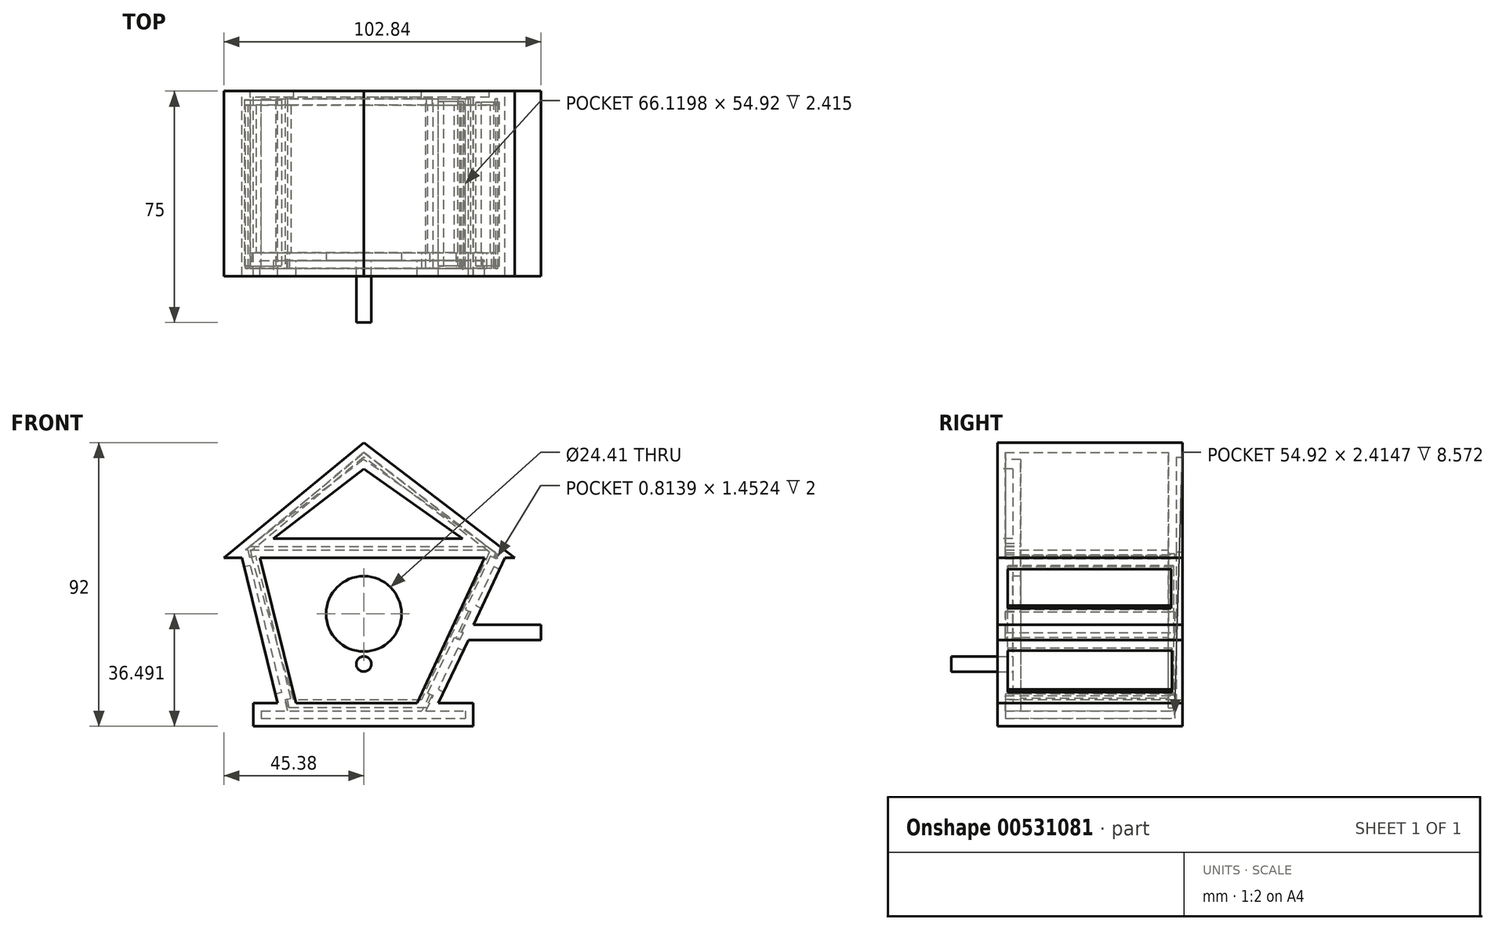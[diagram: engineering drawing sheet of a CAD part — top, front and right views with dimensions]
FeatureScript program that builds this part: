
annotation { "Feature Type Name" : "Feature", "Feature Type Description" : "" }
export const myFeature = defineFeature(function(context is Context, id is Id, definition is map)
    precondition{}
    {
        {
            var Q0;
            Q0=qCreatedBy(makeId("Front.planeOp"),FACE);
            var sketch = newSketch(context, id + "F0", { "sketchPlane" : qUnion([Q0])});
            skLineSegment(sketch, "E0.bottom", {"start": v(-35.75, -20.45) * mm, "end": v(35.45, -20.45) * mm});
            skLineSegment(sketch, "E0.top", {"start": v(-35.75, -27.94) * mm, "end": v(35.45, -27.94) * mm});
            skLineSegment(sketch, "E0.left", {"start": v(-35.75, -20.45) * mm, "end": v(-35.75, -27.94) * mm});
            skLineSegment(sketch, "E0.right", {"start": v(35.45, -20.45) * mm, "end": v(35.45, -27.94) * mm});
            skLineSegment(sketch, "E1", {"start": v(-27.88, -20.45) * mm, "end": v(-39.5, 26.72) * mm});
            skLineSegment(sketch, "E2", {"start": v(-39.5, 26.72) * mm, "end": v(-33.95, 28.09) * mm});
            skLineSegment(sketch, "E3", {"start": v(-33.95, 28.09) * mm, "end": v(-22, -20.45) * mm});
            skLineSegment(sketch, "E4", {"start": v(24.16, -20.45) * mm, "end": v(33.95, 0) * mm});
            skLineSegment(sketch, "E5", {"start": v(33.95, 0) * mm, "end": v(57.46, 0) * mm});
            skLineSegment(sketch, "E6", {"start": v(57.46, 0) * mm, "end": v(57.46, 4.97) * mm});
            skLineSegment(sketch, "E7", {"start": v(57.46, 4.97) * mm, "end": v(35.59, 4.97) * mm});
            skLineSegment(sketch, "E8", {"start": v(35.59, 4.97) * mm, "end": v(46.36, 28.15) * mm});
            skLineSegment(sketch, "E9", {"start": v(46.36, 28.15) * mm, "end": v(40.98, 30.65) * mm});
            skLineSegment(sketch, "E10", {"start": v(40.98, 30.65) * mm, "end": v(17.23, -20.45) * mm});
            skLineSegment(sketch, "E11", {"start": v(-45.38, 26.72) * mm, "end": v(48.97, 26.72) * mm});
            skLineSegment(sketch, "E12", {"start": v(48.97, 26.72) * mm, "end": v(0, 64.06) * mm});
            skLineSegment(sketch, "E13", {"start": v(0, 64.06) * mm, "end": v(-45.38, 26.72) * mm});
            skSolve(sketch);
        }
        {
            var Q0;
            Q0 = qSketchRegion(id + "F0", true);
            extrude(context, id + "F1", {"entities" : qUnion([Q0]), "depth" : 60 * mm, "offsetDistance" : 25.4 * mm});
        }
        {
            var Q0;
            Q0=makeQuery(id+"F1.opExtrude","CAP_FACE",FACE,{"disambiguationData":[OSD([sQuery(id+"F0.wireOp",EDGE,"E0.bottom"),sQuery(id+"F0.wireOp",EDGE,"E0.top"),sQuery(id+"F0.wireOp",EDGE,"E0.left"),sQuery(id+"F0.wireOp",EDGE,"E0.right"),sQuery(id+"F0.wireOp",EDGE,"E1"),sQuery(id+"F0.wireOp",EDGE,"E3"),sQuery(id+"F0.wireOp",EDGE,"E4"),sQuery(id+"F0.wireOp",EDGE,"E5"),sQuery(id+"F0.wireOp",EDGE,"E6"),sQuery(id+"F0.wireOp",EDGE,"E7"),sQuery(id+"F0.wireOp",EDGE,"E8"),sQuery(id+"F0.wireOp",EDGE,"E10"),sQuery(id+"F0.wireOp",EDGE,"E11"),sQuery(id+"F0.wireOp",EDGE,"E12"),sQuery(id+"F0.wireOp",EDGE,"E13")])],"isStart":true});
            var sketch = newSketch(context, id + "F2", { "sketchPlane" : qUnion([Q0])});
            skLineSegment(sketch, "E14", {"start": v(-39.15, 26.72) * mm, "end": v(33.62, 26.72) * mm});
            skLineSegment(sketch, "E15", {"start": v(33.62, 26.72) * mm, "end": v(22, -20.45) * mm});
            skLineSegment(sketch, "E16", {"start": v(22, -20.45) * mm, "end": v(-17.23, -20.45) * mm});
            skLineSegment(sketch, "E17", {"start": v(-17.23, -20.45) * mm, "end": v(-39.15, 26.72) * mm});
            skSolve(sketch);
        }
        {
            var Q0;
            Q0 = qSketchRegion(id + "F2", true);
            extrude(context, id + "F3", {"entities" : qUnion([Q0]), "operationType" : NewBodyOperationType.ADD, "oppositeDirection" : true, "depth" : 55 * mm, "offsetDistance" : 25.4 * mm});
        }
        {
            var Q0;
            Q0=makeQuery(id+"F1.opExtrude","CAP_FACE",FACE,{"disambiguationData":[OSD([sQuery(id+"F0.wireOp",EDGE,"E0.bottom"),sQuery(id+"F0.wireOp",EDGE,"E0.top"),sQuery(id+"F0.wireOp",EDGE,"E0.left"),sQuery(id+"F0.wireOp",EDGE,"E0.right"),sQuery(id+"F0.wireOp",EDGE,"E1"),sQuery(id+"F0.wireOp",EDGE,"E3"),sQuery(id+"F0.wireOp",EDGE,"E4"),sQuery(id+"F0.wireOp",EDGE,"E5"),sQuery(id+"F0.wireOp",EDGE,"E6"),sQuery(id+"F0.wireOp",EDGE,"E7"),sQuery(id+"F0.wireOp",EDGE,"E8"),sQuery(id+"F0.wireOp",EDGE,"E10"),sQuery(id+"F0.wireOp",EDGE,"E11"),sQuery(id+"F0.wireOp",EDGE,"E12"),sQuery(id+"F0.wireOp",EDGE,"E13")])],"isStart":false});
            var sketch = newSketch(context, id + "F4", { "sketchPlane" : qUnion([Q0])});
            skLineSegment(sketch, "E18", {"start": v(-29.38, 32.97) * mm, "end": v(32, 32.97) * mm});
            skLineSegment(sketch, "E19", {"start": v(32, 32.97) * mm, "end": v(0, 55.5) * mm});
            skLineSegment(sketch, "E20", {"start": v(0, 55.5) * mm, "end": v(-29.38, 32.97) * mm});
            skSolve(sketch);
        }
        {
            var Q0;
            Q0 = qSketchRegion(id + "F4", true);
            extrude(context, id + "F5", {"entities" : qUnion([Q0]), "operationType" : NewBodyOperationType.REMOVE, "oppositeDirection" : true, "depth" : 5 * mm, "offsetDistance" : 25.4 * mm});
        }
        {
            var Q0;
            Q0=makeQuery(id+"F1.opExtrude","SWEPT_FACE",FACE,{"disambiguationData":[OSD([sQuery(id+"F0.wireOp",EDGE,"E8")])]});
            var sketch = newSketch(context, id + "F6", { "sketchPlane" : qUnion([Q0])});
            skLineSegment(sketch, "E21.bottom", {"start": v(-56.71, 39.5) * mm, "end": v(-3.67, 39.5) * mm});
            skLineSegment(sketch, "E21.top", {"start": v(-56.71, 25.46) * mm, "end": v(-3.67, 25.46) * mm});
            skLineSegment(sketch, "E21.left", {"start": v(-56.71, 39.5) * mm, "end": v(-56.71, 25.46) * mm});
            skLineSegment(sketch, "E21.right", {"start": v(-3.67, 39.5) * mm, "end": v(-3.67, 25.46) * mm});
            skSolve(sketch);
        }
        {
            var Q0;
            Q0 = qSketchRegion(id + "F6", true);
            extrude(context, id + "F7", {"entities" : qUnion([Q0]), "operationType" : NewBodyOperationType.REMOVE, "oppositeDirection" : true, "depth" : 2 * mm, "offsetDistance" : 25.4 * mm});
        }
        {
            var Q0;
            Q0=makeQuery(id+"F1.opExtrude","SWEPT_FACE",FACE,{"disambiguationData":[OSD([sQuery(id+"F0.wireOp",EDGE,"E4")])]});
            var sketch = newSketch(context, id + "F8", { "sketchPlane" : qUnion([Q0])});
            skLineSegment(sketch, "E22.bottom", {"start": v(-56.72, 10.95) * mm, "end": v(-3.41, 10.95) * mm});
            skLineSegment(sketch, "E22.top", {"start": v(-56.72, -3.97) * mm, "end": v(-3.41, -3.97) * mm});
            skLineSegment(sketch, "E22.left", {"start": v(-56.72, 10.95) * mm, "end": v(-56.72, -3.97) * mm});
            skLineSegment(sketch, "E22.right", {"start": v(-3.41, 10.95) * mm, "end": v(-3.41, -3.97) * mm});
            skSolve(sketch);
        }
        {
            var Q0;
            Q0 = qSketchRegion(id + "F8", true);
            extrude(context, id + "F9", {"entities" : qUnion([Q0]), "operationType" : NewBodyOperationType.REMOVE, "oppositeDirection" : true, "depth" : 2 * mm, "offsetDistance" : 25.4 * mm});
        }
        {
            var Q0;
            Q0=makeQuery(id+"F1.opExtrude","SWEPT_FACE",FACE,{"disambiguationData":[OSD([sQuery(id+"F0.wireOp",EDGE,"E1")])]});
            var sketch = newSketch(context, id + "F10", { "sketchPlane" : qUnion([Q0])});
            skLineSegment(sketch, "E23.bottom", {"start": v(2.9, 32.33) * mm, "end": v(56.77, 32.33) * mm});
            skLineSegment(sketch, "E23.top", {"start": v(2.9, -10.11) * mm, "end": v(56.77, -10.11) * mm});
            skLineSegment(sketch, "E23.left", {"start": v(2.9, 32.33) * mm, "end": v(2.9, -10.11) * mm});
            skLineSegment(sketch, "E23.right", {"start": v(56.77, 32.33) * mm, "end": v(56.77, -10.11) * mm});
            skSolve(sketch);
        }
        {
            var Q0;
            Q0 = qSketchRegion(id + "F10", true);
            extrude(context, id + "F11", {"entities" : qUnion([Q0]), "operationType" : NewBodyOperationType.REMOVE, "oppositeDirection" : true, "depth" : 2 * mm, "offsetDistance" : 25.4 * mm});
        }
        {
            var Q0;
            Q0=makeQuery(id+"F3.boolean.opBoolean","MERGE",FACE,{"derivedFrom":[makeQuery(id+"F1.opExtrude","CAP_FACE",FACE,{"disambiguationData":[OSD([sQuery(id+"F0.wireOp",EDGE,"E0.bottom"),sQuery(id+"F0.wireOp",EDGE,"E0.top"),sQuery(id+"F0.wireOp",EDGE,"E0.left"),sQuery(id+"F0.wireOp",EDGE,"E0.right"),sQuery(id+"F0.wireOp",EDGE,"E1"),sQuery(id+"F0.wireOp",EDGE,"E3"),sQuery(id+"F0.wireOp",EDGE,"E4"),sQuery(id+"F0.wireOp",EDGE,"E5"),sQuery(id+"F0.wireOp",EDGE,"E6"),sQuery(id+"F0.wireOp",EDGE,"E7"),sQuery(id+"F0.wireOp",EDGE,"E8"),sQuery(id+"F0.wireOp",EDGE,"E10"),sQuery(id+"F0.wireOp",EDGE,"E11"),sQuery(id+"F0.wireOp",EDGE,"E12"),sQuery(id+"F0.wireOp",EDGE,"E13")])],"isStart":true}),makeQuery(id+"F3.opExtrude","CAP_FACE",FACE,{"disambiguationData":[OSD([sQuery(id+"F2.wireOp",EDGE,"E14"),sQuery(id+"F2.wireOp",EDGE,"E15"),sQuery(id+"F2.wireOp",EDGE,"E16"),sQuery(id+"F2.wireOp",EDGE,"E17")])],"isStart":true})]});
            var sketch = newSketch(context, id + "F12", { "sketchPlane" : qUnion([Q0])});
            skLineSegment(sketch, "E24", {"start": v(0, 59.38) * mm, "end": v(36.84, 28.57) * mm});
            skLineSegment(sketch, "E25", {"start": v(-40.7, 28.57) * mm, "end": v(0, 59.38) * mm});
            skLineSegment(sketch, "E26", {"start": v(-40.7, 28.57) * mm, "end": v(-18.65, -19.36) * mm});
            skLineSegment(sketch, "E27", {"start": v(-18.65, -19.36) * mm, "end": v(22.7, -19.36) * mm});
            skLineSegment(sketch, "E28", {"start": v(22.7, -19.36) * mm, "end": v(36.84, 28.57) * mm});
            skSolve(sketch);
        }
        {
            var Q0;
            Q0 = qSketchRegion(id + "F12", true);
            extrude(context, id + "F13", {"entities" : qUnion([Q0]), "operationType" : NewBodyOperationType.REMOVE, "oppositeDirection" : true, "depth" : 2 * mm, "offsetDistance" : 25.4 * mm});
        }
        {
            var Q0;
            Q0=makeQuery(id+"F3.opExtrude","CAP_FACE",FACE,{"disambiguationData":[OSD([sQuery(id+"F2.wireOp",EDGE,"E14"),sQuery(id+"F2.wireOp",EDGE,"E15"),sQuery(id+"F2.wireOp",EDGE,"E16"),sQuery(id+"F2.wireOp",EDGE,"E17")])],"isStart":false});
            var sketch = newSketch(context, id + "F14", { "sketchPlane" : qUnion([Q0])});
            skCircle(sketch, "E29", {"center": v(0, 8.55) * mm, "radius": 12.2 * mm});
            skSolve(sketch);
        }
        {
            var Q0;
            Q0 = qSketchRegion(id + "F14", true);
            extrude(context, id + "F15", {"entities" : qUnion([Q0]), "operationType" : NewBodyOperationType.REMOVE, "oppositeDirection" : true, "depth" : 60 * mm, "offsetDistance" : 25.4 * mm});
        }
        {
            var Q0;
            Q0=makeQuery(id+"F15.boolean.opBoolean","COPY",FACE,{"derivedFrom":makeQuery(id+"F15.opExtrude","SWEPT_FACE",FACE,{"disambiguationData":[OSD([sQuery(id+"F14.wireOp",EDGE,"E29")])]})});
            shell(context, id + "F16", {"entities" : qUnion([Q0]), "thickness" : 2.54 * mm});
        }
        {
            var Q0;
            Q0=makeQuery(id+"F13.boolean.opBoolean","COPY",FACE,{"derivedFrom":makeQuery(id+"F13.opExtrude","CAP_FACE",FACE,{"disambiguationData":[OSD([sQuery(id+"F12.wireOp",EDGE,"E24"),sQuery(id+"F12.wireOp",EDGE,"E25"),sQuery(id+"F12.wireOp",EDGE,"E26"),sQuery(id+"F12.wireOp",EDGE,"E27"),sQuery(id+"F12.wireOp",EDGE,"E28")])],"isStart":false})});
            var sketch = newSketch(context, id + "F17", { "sketchPlane" : qUnion([Q0])});
            skCircle(sketch, "E30", {"center": v(0, 8.55) * mm, "radius": 13.38 * mm});
            skSolve(sketch);
        }
        {
            var Q0;
            Q0 = qSketchRegion(id + "F17", true);
            extrude(context, id + "F18", {"entities" : qUnion([Q0]), "operationType" : NewBodyOperationType.ADD, "oppositeDirection" : true, "depth" : 3 * mm, "offsetDistance" : 25.4 * mm});
        }
        {
            var Q0;
            Q0=makeQuery(id+"F3.opExtrude","CAP_FACE",FACE,{"disambiguationData":[OSD([sQuery(id+"F2.wireOp",EDGE,"E14"),sQuery(id+"F2.wireOp",EDGE,"E15"),sQuery(id+"F2.wireOp",EDGE,"E16"),sQuery(id+"F2.wireOp",EDGE,"E17")])],"isStart":false});
            var sketch = newSketch(context, id + "F19", { "sketchPlane" : qUnion([Q0])});
            skCircle(sketch, "E31", {"center": v(0, -7.73) * mm, "radius": 2.45 * mm});
            skSolve(sketch);
        }
        {
            var Q0;
            Q0 = qSketchRegion(id + "F19", true);
            extrude(context, id + "F20", {"entities" : qUnion([Q0]), "operationType" : NewBodyOperationType.ADD, "depth" : 20 * mm, "offsetDistance" : 25.4 * mm});
        }
        {
            var Q0;
            Q0=makeQuery(id+"F16.opShell","OFFSET_FACE",FACE,{"disambiguationData":[OSD([sQuery(id+"F12.wireOp",EDGE,"E24"),sQuery(id+"F12.wireOp",EDGE,"E25"),sQuery(id+"F12.wireOp",EDGE,"E26"),sQuery(id+"F12.wireOp",EDGE,"E27"),sQuery(id+"F12.wireOp",EDGE,"E28")])]});
            var sketch = newSketch(context, id + "F21", { "sketchPlane" : qUnion([Q0])});
            skLineSegment(sketch, "E32.bottom", {"start": v(-14.74, 22.93) * mm, "end": v(16.99, 22.93) * mm});
            skLineSegment(sketch, "E32.top", {"start": v(-14.74, -4.89) * mm, "end": v(16.99, -4.89) * mm});
            skLineSegment(sketch, "E32.left", {"start": v(-14.74, 22.93) * mm, "end": v(-14.74, -4.89) * mm});
            skLineSegment(sketch, "E32.right", {"start": v(16.99, 22.93) * mm, "end": v(16.99, -4.89) * mm});
            skSolve(sketch);
        }
        {
            var Q0;
            Q0 = qSketchRegion(id + "F21", true);
            extrude(context, id + "F22", {"entities" : qUnion([Q0]), "operationType" : NewBodyOperationType.REMOVE, "depth" : 25.4 * mm, "offsetDistance" : 25.4 * mm});
        }
    });
